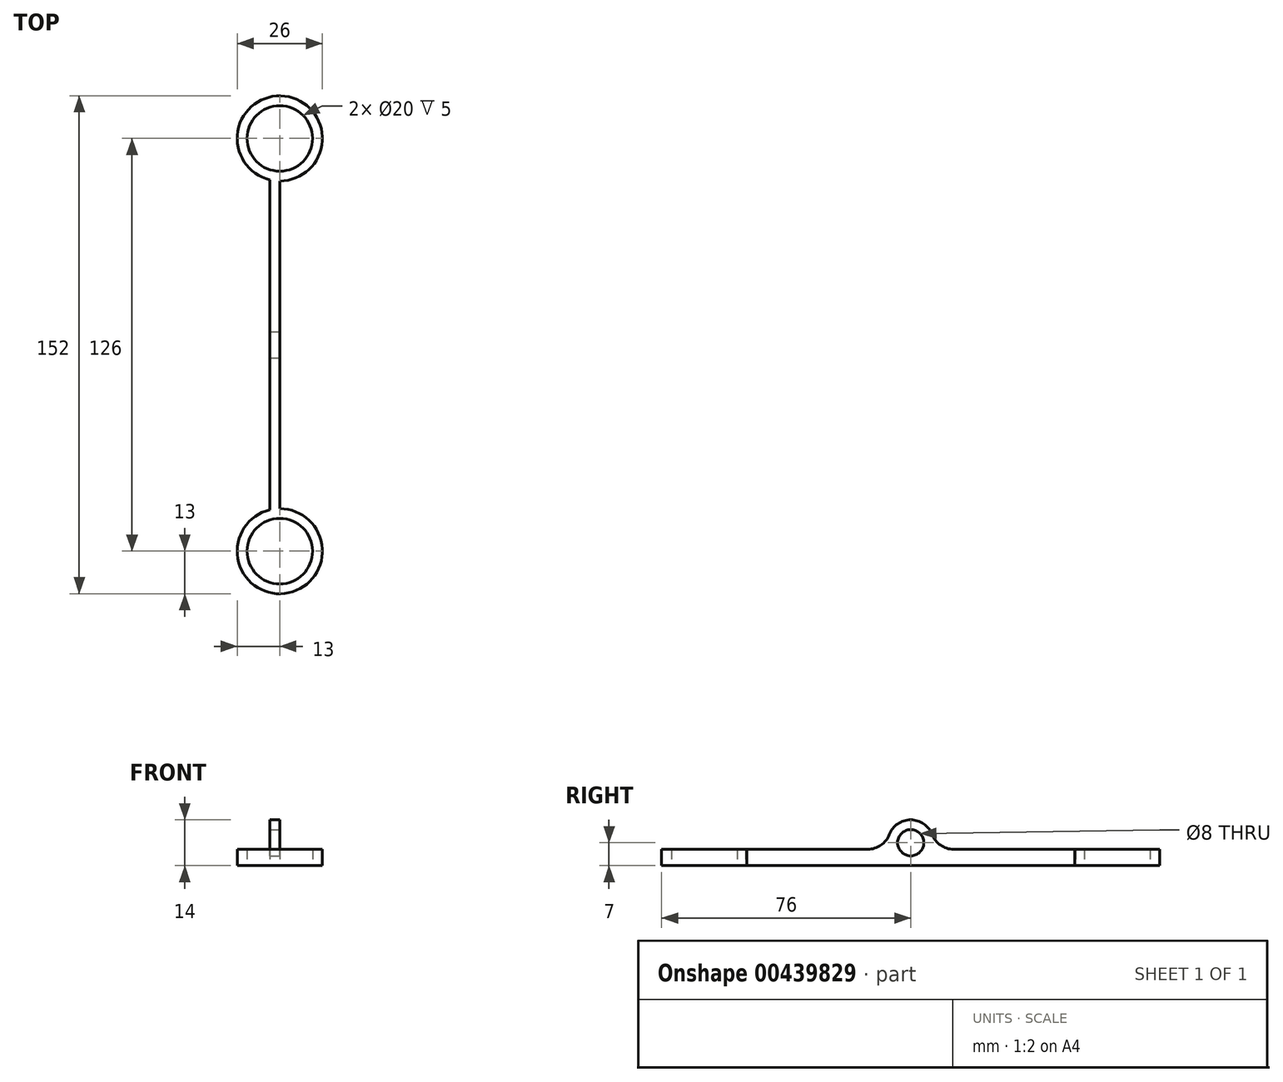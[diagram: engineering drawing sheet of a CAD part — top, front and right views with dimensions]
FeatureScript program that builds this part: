
annotation { "Feature Type Name" : "Feature", "Feature Type Description" : "" }
export const myFeature = defineFeature(function(context is Context, id is Id, definition is map)
    precondition{}
    {
        {
            var Q0;
            Q0=qCreatedBy(makeId("Top.planeOp"),FACE);
            var sketch = newSketch(context, id + "F0", { "sketchPlane" : qUnion([Q0])});
            skArc(sketch, "E0", {"start": v(-3, -50.35) * mm, "mid": v(1.51, -75.91) * mm, "end": v(0, -50) * mm});
            skArc(sketch, "E1", {"start": v(0, 50) * mm, "mid": v(1.51, 75.91) * mm, "end": v(-3, 50.35) * mm});
            skLineSegment(sketch, "E2.left", {"start": v(-3, 50.35) * mm, "end": v(-3, -50.35) * mm});
            skLineSegment(sketch, "E2.right", {"start": v(0, 50) * mm, "end": v(0, -50) * mm});
            skPoint(sketch, "E2.middle", {"position": v(0, 0) * mm});
            skLineSegment(sketch, "E3", {"start": v(0, -63) * mm, "end": v(0, 63) * mm, "construction": true});
            skCircle(sketch, "E4", {"center": v(0, 63) * mm, "radius": 10 * mm});
            skCircle(sketch, "E5", {"center": v(0, -63) * mm, "radius": 10 * mm});
            skSolve(sketch);
        }
        {
            var Q0;
            Q0=makeQuery(id+"F0.imprint","IMPRINT",FACE,{"disambiguationData":[TD([[makeQuery(id+"F0.imprint","IMPRINT",EDGE,{"derivedFrom":sQuery(id+"F0.wireOp",EDGE,"E0")}),1.0]])]});
            extrude(context, id + "F1", {"entities" : qUnion([Q0]), "endBound" : BoundingType.SYMMETRIC, "depth" : 5 * mm});
        }
        {
            var Q0;
            Q0=makeQuery(id+"F1.opExtrude","SWEPT_FACE",FACE,{"disambiguationData":[OSD([sQuery(id+"F0.wireOp",EDGE,"E2.right")])]});
            var sketch = newSketch(context, id + "F2", { "sketchPlane" : qUnion([Q0])});
            skCircle(sketch, "E6", {"center": v(0, 4.5) * mm, "radius": 4 * mm});
            skArc(sketch, "E7", {"start": v(-13.08, 2.5) * mm, "mid": v(-9.1, 3.73) * mm, "end": v(-6.54, 7) * mm});
            skArc(sketch, "E8", {"start": v(6.54, 7) * mm, "mid": v(9.1, 3.73) * mm, "end": v(13.08, 2.5) * mm});
            skArc(sketch, "E9.trimOffspring", {"start": v(6.54, 7) * mm, "mid": v(0, 11.5) * mm, "end": v(-6.54, 7) * mm});
            skLineSegment(sketch, "E10", {"start": v(-13.08, -2.5) * mm, "end": v(-13.08, 2.5) * mm});
            skLineSegment(sketch, "E11", {"start": v(13.08, 2.5) * mm, "end": v(13.08, -2.5) * mm});
            skArc(sketch, "E12", {"start": v(-6.54, 7) * mm, "mid": v(0, -2.5) * mm, "end": v(6.54, 7) * mm, "construction": true});
            skSolve(sketch);
        }
        {
            var Q0;
            {var subQ1=sQuery(id+"F2.wireOp",EDGE,"E7");Q0=makeQuery(id+"F2.imprint","IMPRINT",FACE,{"disambiguationData":[TD([[makeQuery(id+"F2.imprint","IMPRINT",EDGE,{"derivedFrom":subQ1}),-1.0]])]});}
            var Q1;
            Q1=makeQuery(id+"F2.imprint","IMPRINT",FACE,{"disambiguationData":[TD([[makeQuery(id+"F2.imprint","IMPRINT",EDGE,{"derivedFrom":sQuery(id+"F2.wireOp",EDGE,"qWw3OOI6-yzFZ-2gxW-cSai-WMPe5i8k7zR8")}),1.0]])]});
            var Q2;
            {var subQ6=sQuery(id+"F2.wireOp",EDGE,"E10");Q2=makeQuery(id+"F2.imprint","IMPRINT",FACE,{"disambiguationData":[TD([[makeQuery(id+"F2.imprint","IMPRINT",EDGE,{"derivedFrom":subQ6}),-1.0]])]});}
            var Q3;
            {var subQ6=sQuery(id+"F2.wireOp",EDGE,"E11");Q3=makeQuery(id+"F2.imprint","IMPRINT",FACE,{"disambiguationData":[TD([[makeQuery(id+"F2.imprint","IMPRINT",EDGE,{"derivedFrom":subQ6}),-1.0]])]});}
            var Q4;
            Q4=makeQuery(id+"F1.opExtrude","SWEPT_FACE",FACE,{"disambiguationData":[OSD([sQuery(id+"F0.wireOp",EDGE,"E2.left")])]});
            extrude(context, id + "F3", {"entities" : qUnion([Q0, Q1, Q2, Q3]), "operationType" : NewBodyOperationType.ADD, "endBound" : BoundingType.UP_TO_SURFACE, "oppositeDirection" : true, "endBoundEntityFace" : qUnion([Q4]), "depth" : 25 * mm});
        }
        {
            var Q0;
            {var subQ0=sQuery(id+"F2.wireOp",EDGE,"E6");var subQ1=sQuery(id+"F0.wireOp",EDGE,"E2.right");var subQ2=makeQuery(id+"F1.opExtrude","CAP_EDGE",EDGE,{"disambiguationData":[OSD([subQ1])],"isStart":false});var subQ3=makeQuery(id+"F2.imprint","INTERSECT",VERTEX,{"disambiguationData":[OD(0.0)],"derivedFrom":[subQ2,subQ0]});Q0=makeQuery(id+"F2.imprint","IMPRINT",FACE,{"disambiguationData":[TD([[makeQuery(id+"F2.imprint","IMPRINT",EDGE,{"disambiguationData":[TD([[subQ3,-1.0]])],"derivedFrom":subQ0}),1.0]])]});}
            extrude(context, id + "F4", {"entities" : qUnion([Q0]), "operationType" : NewBodyOperationType.REMOVE, "oppositeDirection" : true, "depth" : 25 * mm});
        }
    });
